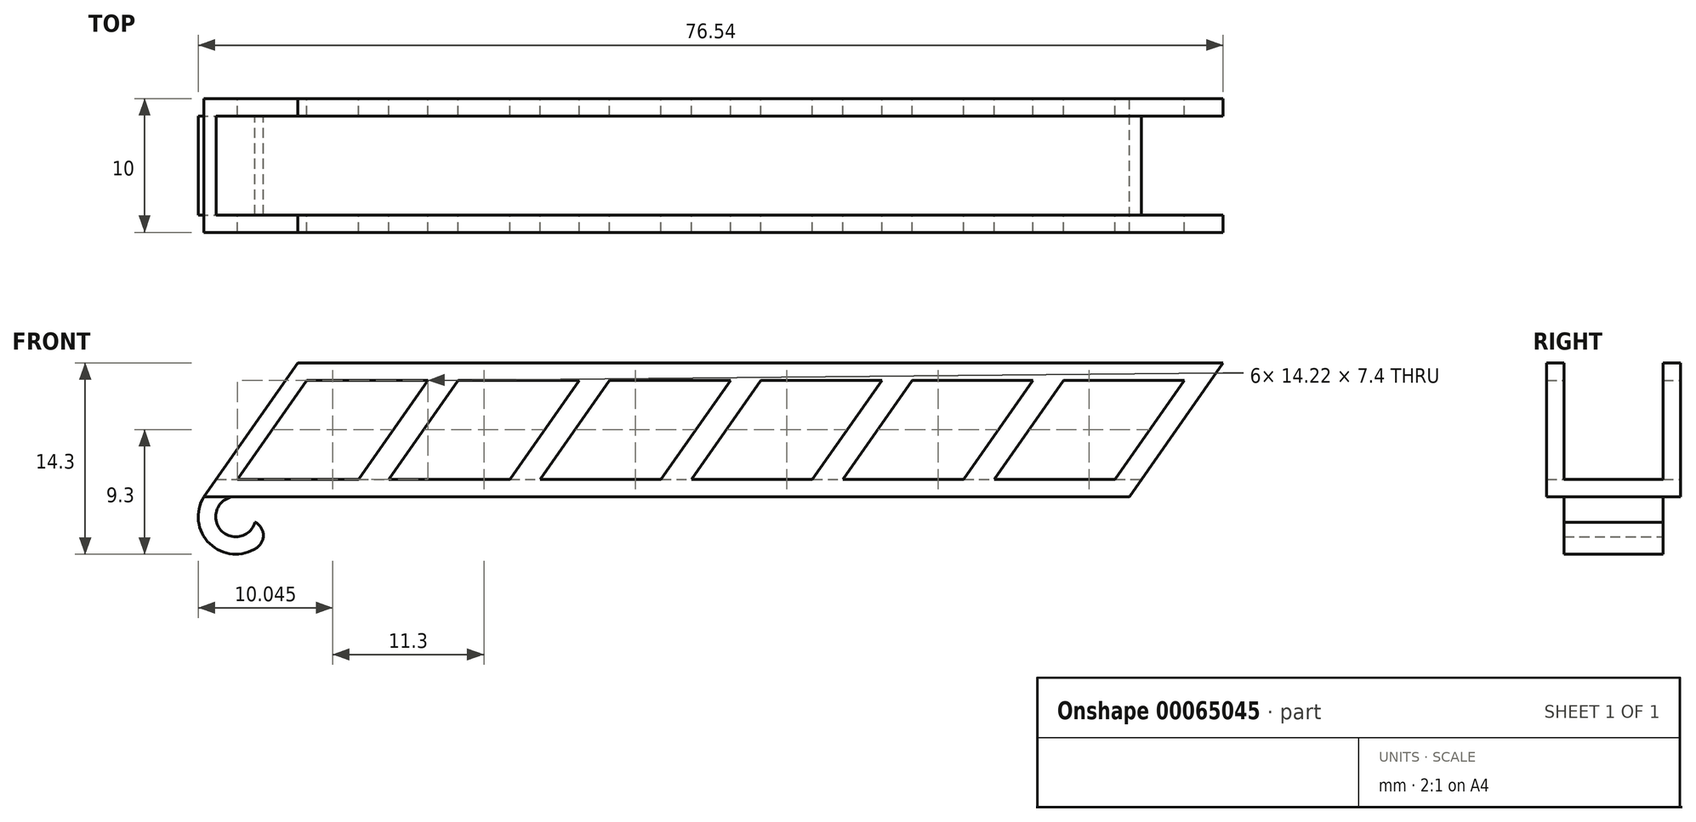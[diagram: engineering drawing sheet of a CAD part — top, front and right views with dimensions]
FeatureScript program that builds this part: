
annotation { "Feature Type Name" : "Feature", "Feature Type Description" : "" }
export const myFeature = defineFeature(function(context is Context, id is Id, definition is map)
    precondition{}
    {
        {
            assignVariable(context, id + "F0", {"name" : "Width", "anyValue" : 10});
        }
        {
            assignVariable(context, id + "F1", {"name" : "FrameWidth", "anyValue" : 1.3});
        }
        {
            var Q0;
            Q0=qCreatedBy(makeId("Front.planeOp"),FACE);
            var sketch = newSketch(context, id + "F2", { "sketchPlane" : qUnion([Q0])});
            skLineSegment(sketch, "E0", {"start": v(0, 0) * mm, "end": v(69.1, 0) * mm});
            skLineSegment(sketch, "E1", {"start": v(69.1, 0) * mm, "end": v(76.1, 10) * mm});
            skLineSegment(sketch, "E2", {"start": v(76.1, 10) * mm, "end": v(7, 10) * mm});
            skLineSegment(sketch, "E3", {"start": v(7, 10) * mm, "end": v(0, 0) * mm});
            skLineSegment(sketch, "E4", {"start": v(7.68, 8.7) * mm, "end": v(2.5, 1.3) * mm});
            skLineSegment(sketch, "E5", {"start": v(7.68, 8.7) * mm, "end": v(16.71, 8.7) * mm});
            skLineSegment(sketch, "E6", {"start": v(16.71, 8.7) * mm, "end": v(11.53, 1.3) * mm});
            skLineSegment(sketch, "E7", {"start": v(11.53, 1.3) * mm, "end": v(2.5, 1.3) * mm});
            skLineSegment(sketch, "E8.1.0.0", {"start": v(22.83, 1.3) * mm, "end": v(13.8, 1.3) * mm});
            skLineSegment(sketch, "E8.1.0.1", {"start": v(18.98, 8.7) * mm, "end": v(13.8, 1.3) * mm});
            skLineSegment(sketch, "E8.1.0.2", {"start": v(18.98, 8.7) * mm, "end": v(28.01, 8.7) * mm});
            skLineSegment(sketch, "E8.1.0.3", {"start": v(28.01, 8.7) * mm, "end": v(22.83, 1.3) * mm});
            skLineSegment(sketch, "E8.2.0.0", {"start": v(34.13, 1.3) * mm, "end": v(25.1, 1.3) * mm});
            skLineSegment(sketch, "E8.2.0.1", {"start": v(30.28, 8.7) * mm, "end": v(25.1, 1.3) * mm});
            skLineSegment(sketch, "E8.2.0.2", {"start": v(30.28, 8.7) * mm, "end": v(39.31, 8.7) * mm});
            skLineSegment(sketch, "E8.2.0.3", {"start": v(39.31, 8.7) * mm, "end": v(34.13, 1.3) * mm});
            skLineSegment(sketch, "E8.3.0.0", {"start": v(45.43, 1.3) * mm, "end": v(36.4, 1.3) * mm});
            skLineSegment(sketch, "E8.3.0.1", {"start": v(41.58, 8.7) * mm, "end": v(36.4, 1.3) * mm});
            skLineSegment(sketch, "E8.3.0.2", {"start": v(41.58, 8.7) * mm, "end": v(50.61, 8.7) * mm});
            skLineSegment(sketch, "E8.3.0.3", {"start": v(50.61, 8.7) * mm, "end": v(45.43, 1.3) * mm});
            skLineSegment(sketch, "E8.4.0.0", {"start": v(56.73, 1.3) * mm, "end": v(47.7, 1.3) * mm});
            skLineSegment(sketch, "E8.4.0.1", {"start": v(52.88, 8.7) * mm, "end": v(47.7, 1.3) * mm});
            skLineSegment(sketch, "E8.4.0.2", {"start": v(52.88, 8.7) * mm, "end": v(61.91, 8.7) * mm});
            skLineSegment(sketch, "E8.4.0.3", {"start": v(61.91, 8.7) * mm, "end": v(56.73, 1.3) * mm});
            skLineSegment(sketch, "E8.direction1", {"start": v(2.5, 1.3) * mm, "end": v(13.8, 1.3) * mm, "construction": true});
            skLineSegment(sketch, "E9.0.5.0", {"start": v(68.03, 1.3) * mm, "end": v(59, 1.3) * mm});
            skLineSegment(sketch, "E9.3.5.0", {"start": v(64.18, 8.7) * mm, "end": v(59, 1.3) * mm});
            skLineSegment(sketch, "E9.6.5.0", {"start": v(64.18, 8.7) * mm, "end": v(73.21, 8.7) * mm});
            skLineSegment(sketch, "E9.9.5.0", {"start": v(73.21, 8.7) * mm, "end": v(68.03, 1.3) * mm});
            skCircle(sketch, "E10", {"center": v(2.36, -1.5) * mm, "radius": 1.5 * mm});
            skCircle(sketch, "E11", {"center": v(2.36, -1.5) * mm, "radius": 2.8 * mm});
            skLineSegment(sketch, "E12", {"start": v(0, 0) * mm, "end": v(4.98, -2.5) * mm});
            skSolve(sketch);
        }
        {
            var Q0;
            Q0=makeQuery(id+"F2.imprint","IMPRINT",FACE,{"disambiguationData":[TD([[makeQuery(id+"F2.imprint","IMPRINT",EDGE,{"derivedFrom":sQuery(id+"F2.wireOp",EDGE,"E4")}),1.0]])]});
            var Q1;
            Q1=makeQuery(id+"F2.imprint","IMPRINT",FACE,{"disambiguationData":[TD([[makeQuery(id+"F2.imprint","IMPRINT",EDGE,{"derivedFrom":sQuery(id+"F2.wireOp",EDGE,"E8.1.0.0")}),-1.0]])]});
            var Q2;
            Q2=makeQuery(id+"F2.imprint","IMPRINT",FACE,{"disambiguationData":[TD([[makeQuery(id+"F2.imprint","IMPRINT",EDGE,{"derivedFrom":sQuery(id+"F2.wireOp",EDGE,"E8.3.0.0")}),-1.0]])]});
            var Q3;
            Q3=makeQuery(id+"F2.imprint","IMPRINT",FACE,{"disambiguationData":[TD([[makeQuery(id+"F2.imprint","IMPRINT",EDGE,{"derivedFrom":sQuery(id+"F2.wireOp",EDGE,"E8.4.0.0")}),-1.0]])]});
            var Q4;
            Q4=makeQuery(id+"F2.imprint","IMPRINT",FACE,{"disambiguationData":[TD([[makeQuery(id+"F2.imprint","IMPRINT",EDGE,{"derivedFrom":sQuery(id+"F2.wireOp",EDGE,"E9.0.5.0")}),-1.0]])]});
            var Q5;
            Q5=makeQuery(id+"F2.imprint","IMPRINT",FACE,{"disambiguationData":[TD([[makeQuery(id+"F2.imprint","IMPRINT",EDGE,{"derivedFrom":sQuery(id+"F2.wireOp",EDGE,"E8.2.0.0")}),-1.0]])]});
            var Q6;
            {var subQ4=sQuery(id+"F2.wireOp",EDGE,"E1");Q6=makeQuery(id+"F2.imprint","IMPRINT",FACE,{"disambiguationData":[TD([[makeQuery(id+"F2.imprint","IMPRINT",EDGE,{"derivedFrom":subQ4}),1.0]])]});}
            var Q7;
            {var subQ0=sQuery(id+"F2.wireOp",EDGE,"E11");var subQ2=sQuery(id+"F2.wireOp",EDGE,"E0");var subQ5=makeQuery(id+"F2.imprint","INTERSECT",VERTEX,{"derivedFrom":[subQ2,subQ0]});Q7=makeQuery(id+"F2.imprint","IMPRINT",FACE,{"disambiguationData":[TD([[makeQuery(id+"F2.imprint","IMPRINT",EDGE,{"disambiguationData":[TD([[subQ5,1.0]])],"derivedFrom":subQ2}),1.0]])]});}
            extrude(context, id + "F3", {"entities" : qUnion([Q0, Q1, Q2, Q3, Q4, Q5, Q6, Q7]), "depth" : (getVariable(context, 'Width')) * mm});
        }
        {
            var Q0;
            Q0=makeQuery(id+"F3.opExtrude","SWEPT_FACE",FACE,{"disambiguationData":[OSD([sQuery(id+"F2.wireOp",EDGE,"E3")])]});
            var Q1;
            Q1=makeQuery(id+"F3.opExtrude","SWEPT_FACE",FACE,{"disambiguationData":[OSD([sQuery(id+"F2.wireOp",EDGE,"E2")])]});
            var Q2;
            Q2=makeQuery(id+"F3.opExtrude","SWEPT_FACE",FACE,{"disambiguationData":[OSD([sQuery(id+"F2.wireOp",EDGE,"E1")])]});
            shell(context, id + "F4", {"entities" : qUnion([Q0, Q1, Q2]), "thickness" : (getVariable(context, 'FrameWidth')) * mm});
        }
        {
            var Q0;
            {var subQ1=sQuery(id+"F2.wireOp",EDGE,"E0");var subQ3=sQuery(id+"F2.wireOp",EDGE,"E10");var subQ4=makeQuery(id+"F2.imprint","INTERSECT",VERTEX,{"derivedFrom":[subQ1,subQ3]});Q0=makeQuery(id+"F2.imprint","IMPRINT",FACE,{"disambiguationData":[TD([[makeQuery(id+"F2.imprint","IMPRINT",EDGE,{"disambiguationData":[TD([[subQ4,-1.0]])],"derivedFrom":subQ3}),-1.0]])]});}
            var Q1;
            {var subQ0=sQuery(id+"F2.wireOp",EDGE,"E12");var subQ1=sQuery(id+"F2.wireOp",EDGE,"E10");var subQ2=makeQuery(id+"F2.imprint","INTERSECT",VERTEX,{"disambiguationData":[OD(0.0)],"derivedFrom":[subQ1,subQ0]});Q1=makeQuery(id+"F2.imprint","IMPRINT",FACE,{"disambiguationData":[TD([[makeQuery(id+"F2.imprint","IMPRINT",EDGE,{"disambiguationData":[TD([[subQ2,-1.0]])],"derivedFrom":subQ1}),-1.0]])]});}
            extrude(context, id + "F5", {"entities" : qUnion([Q0, Q1]), "operationType" : NewBodyOperationType.ADD, "depth" : (getVariable(context, 'Width') - getVariable(context, 'FrameWidth')) * mm, "hasSecondDirection" : true, "secondDirectionOppositeDirection" : false, "secondDirectionDepth" : (getVariable(context, 'FrameWidth')) * mm});
        }
        {
            var Q0;
            Q0=makeQuery(id+"F2.imprint","IMPRINT",FACE,{"disambiguationData":[TD([[makeQuery(id+"F2.imprint","IMPRINT",EDGE,{"derivedFrom":sQuery(id+"F2.wireOp",EDGE,"E9.0.5.0")}),-1.0]])]});
            var Q1;
            Q1=makeQuery(id+"F2.imprint","IMPRINT",FACE,{"disambiguationData":[TD([[makeQuery(id+"F2.imprint","IMPRINT",EDGE,{"derivedFrom":sQuery(id+"F2.wireOp",EDGE,"E8.4.0.0")}),-1.0]])]});
            var Q2;
            Q2=makeQuery(id+"F2.imprint","IMPRINT",FACE,{"disambiguationData":[TD([[makeQuery(id+"F2.imprint","IMPRINT",EDGE,{"derivedFrom":sQuery(id+"F2.wireOp",EDGE,"E8.3.0.0")}),-1.0]])]});
            var Q3;
            Q3=makeQuery(id+"F2.imprint","IMPRINT",FACE,{"disambiguationData":[TD([[makeQuery(id+"F2.imprint","IMPRINT",EDGE,{"derivedFrom":sQuery(id+"F2.wireOp",EDGE,"E8.2.0.0")}),-1.0]])]});
            var Q4;
            Q4=makeQuery(id+"F2.imprint","IMPRINT",FACE,{"disambiguationData":[TD([[makeQuery(id+"F2.imprint","IMPRINT",EDGE,{"derivedFrom":sQuery(id+"F2.wireOp",EDGE,"E8.1.0.0")}),-1.0]])]});
            var Q5;
            Q5=makeQuery(id+"F2.imprint","IMPRINT",FACE,{"disambiguationData":[TD([[makeQuery(id+"F2.imprint","IMPRINT",EDGE,{"derivedFrom":sQuery(id+"F2.wireOp",EDGE,"E4")}),1.0]])]});
            extrude(context, id + "F6", {"entities" : qUnion([Q0, Q1, Q2, Q3, Q4, Q5]), "operationType" : NewBodyOperationType.REMOVE, "endBound" : BoundingType.THROUGH_ALL, "depth" : 25 * mm});
        }
        {
            var Q0;
            {var subQ0=sQuery(id+"F2.wireOp",EDGE,"E12");var subQ1=sQuery(id+"F2.wireOp",EDGE,"E11");var subQ2=sQuery(id+"F2.wireOp",EDGE,"E10");Q0=makeQuery(id+"Fxm5VyiRL0xjojC_1.boolean.opBoolean","SPLIT",EDGE,{"disambiguationData":[TD([makeQuery(id+"Fxm5VyiRL0xjojC_1.opExtrude","CAP_FACE",FACE,{"disambiguationData":[OSD([subQ2,subQ1,subQ0])],"isStart":false})])],"derivedFrom":makeQuery(id+"F5.opExtrude","SWEPT_EDGE",EDGE,{"disambiguationData":[OSD([subQ1,subQ0])]})});}
            var Q1;
            {var subQ0=sQuery(id+"F2.wireOp",EDGE,"E12");var subQ1=sQuery(id+"F2.wireOp",EDGE,"E11");var subQ2=sQuery(id+"F2.wireOp",EDGE,"E10");Q1=makeQuery(id+"Fxm5VyiRL0xjojC_1.boolean.opBoolean","SPLIT",EDGE,{"disambiguationData":[TD([makeQuery(id+"Fxm5VyiRL0xjojC_1.opExtrude","CAP_FACE",FACE,{"disambiguationData":[OSD([subQ2,subQ1,subQ0])],"isStart":true})])],"derivedFrom":makeQuery(id+"F5.opExtrude","SWEPT_EDGE",EDGE,{"disambiguationData":[OSD([subQ1,subQ0])]})});}
            fillet(context, id + "F7", {"entities" : qUnion([Q0, Q1]), "radius" : 1.1 * mm, "tangentPropagation" : true, "allowEdgeOverflow" : false});
        }
    });
